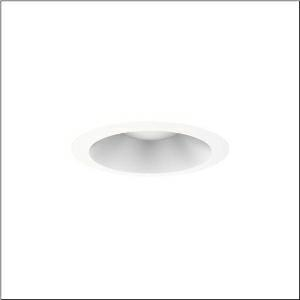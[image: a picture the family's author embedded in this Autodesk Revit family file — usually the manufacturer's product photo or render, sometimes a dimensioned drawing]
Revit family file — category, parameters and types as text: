
# Revit family: lunis_31-xl_51dn16eg42b
name_source: partatom
category: Lighting Fixtures
units: mm (PartAtom-declared; Revit-internal decimal feet)

## family parameters
Cut with Voids When Loaded = No
Host = Face
Light Source = No
Part Type = Normal
Room Calculation Point = No
Round Connector Dimension = Use Diameter
Shared = No

## types (1)
- --- (1 x LED, 2550 lm, 17 W, 4000K)
    Apparent Load = 17 VA
    CIE Flux Codes = 64 93 99 100 100
    Color Rendering = 80
    Color Temperature = 4000K
    Default Elevation = 1800 mm
    Description = Lunis 31-XL, downlight, light control with reflector, light emission: direct distribution, LED rated luminous flux: 2.550lm, light colour: 840, mains connection: 220..240V, AC/DC, 0/50..60Hz, housing, of aluminium, white, protection rating (complete): IP20, protection rating (on room side): IP54, insulation class (complete): insulation class II (safety insulation), certification: CE, ENEC, packaging unit: 1 piece
    Height = 0 mm  [stored 0 ft]
    Lamp = 1 x LED
    Lamp Light Flux = 2550 lm
    Lamp Power = 17 W
    Lamp count = 1
    Length = 259 mm
    Luminous efficacy = 150 lm/W
    Manufacturer = Siteco
    ModVariant = No
    Model = 51DN16EG42B
    Mounting Place = Ceiling
    Mounting Type = Recessed
    Number of Poles = 1
    OnlyDefault = Yes
    Power Factor = 1
    Product Name = Lunis 31-XL
    Product group = downlight
    ProductGroupID = 401
    Protection Class = Protection class II
    Protection Degree = IP 20
    RLX_Detail_Level = 1
    RLX_Emergency_Light_Flux = 0 lm
    RLX_Emergency_Type = 0
    RLX_Emergency_Type_DB = No
    RlxData = <blob elided: 24349 chars, md5=41d3d524>
    Socket = socket
    Standby Power = 0 W
    System Light Flux = 2550 lm
    System Power = 17 W
    Type Comments = individual setting: luminous flux: 100 % | (ON | OFF | ON) | 450 mA
    Type Image = l_1345915.jpg
    URL = http://relux.com
    VarID = @adj_029635
    Voltage = 0 V
    Weight = 0.00 kg
    Width = 0 mm  [stored 0 ft]

note: [stored X ft] marks values corroborated as IEEE doubles in the binary element streams (Revit-internal decimal feet)

## geometry (parser evidence)
native form markers: Blend x4, Sweep x9
no freeform markers — native parametric forms only
